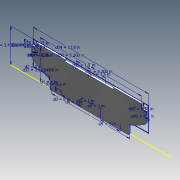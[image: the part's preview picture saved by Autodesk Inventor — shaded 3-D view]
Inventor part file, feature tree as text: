
AUTODESK INVENTOR PART (.ipt)
format: ipt  version: 2020.3 (Build 243373000, 373)  size: 193,536 bytes
history: native  units: in
note: dims shown in document units (in); Inventor stores cm internally (conversion verified against a paired STEP export)
features: extrude x3, hole x3, fillet x3, sketch x2, chamfer x2, projected_geometry x1
ambient origin geometry x8: Origin, YZ Plane, XZ Plane, XY Plane, X Axis, Y Axis, Z Axis, Center Point
bodies: Solid1 (feature_tree)
feature tree (14):
  extrude  "Extrusion1"  Depth=1.0in
  hole  "Hole1"  [1 undecoded]
  hole  "Hole2"  [1 undecoded]
  sketch  "Sketch2"  dims[d0=8.0in d1=1.0in]
  extrude  "Extrusion2"  Depth=0.25in
  hole  "Hole3"  [1 undecoded]
  extrude  "Extrusion3"  Depth=2.0in
  fillet  "Fillet1"  Radius=0.177in
  chamfer  "Chamfer1"  Distance=5.2in
  chamfer  "Chamfer2"  Distance=5.2in
  fillet  "Fillet2"  Radius=3.143in
  fillet  "Fillet3"  Radius=3.45in
  projected_geometry  "Projected Loop1"
  sketch  "Sketch3"  dims[d2=0.0in d5=1.0in d6=2.0in d7=0.3in d8=1.0in d9=2.0in d10=0.177in d11=0.0in d12=0.123in d13=0.75in d14=0.375in d15=0.25in d16=0.5635in d17=1.0in d18=0.8108in d22=0.15in d23=0.75in d24=0.281in d25=0.138in d26=0.5635in d27=1.0in d28=0.8108in d30=5.2in d31=5.2in d32=3.143in d33=3.45in d34=11.8in d35=0.45in d36=0.5in d37=0.22in d38=0.0in d39=0.325in d40=0.2in d41=0.2in d42=0.15in d43=0.75in d44=0.281in d45=0.138in d46=0.5635in d47=1.0in d48=0.8108in d49=0.18in d50=5.0in d51=0.22in d52=0.0in d53=0.25in d54=1.5in d55=0.125in d56=30.0deg d57=1.5in d58=0.125in d59=30.0deg d60=0.5in d61=0.25in d62=1.5in d63=1.5in d64=0.25in d65=0.25in]
note: 3 required parameter values undecoded (feature->parameter linkage not recoverable at this tier; creation-order binding heuristic only, values carry confidence <= 0.55)
